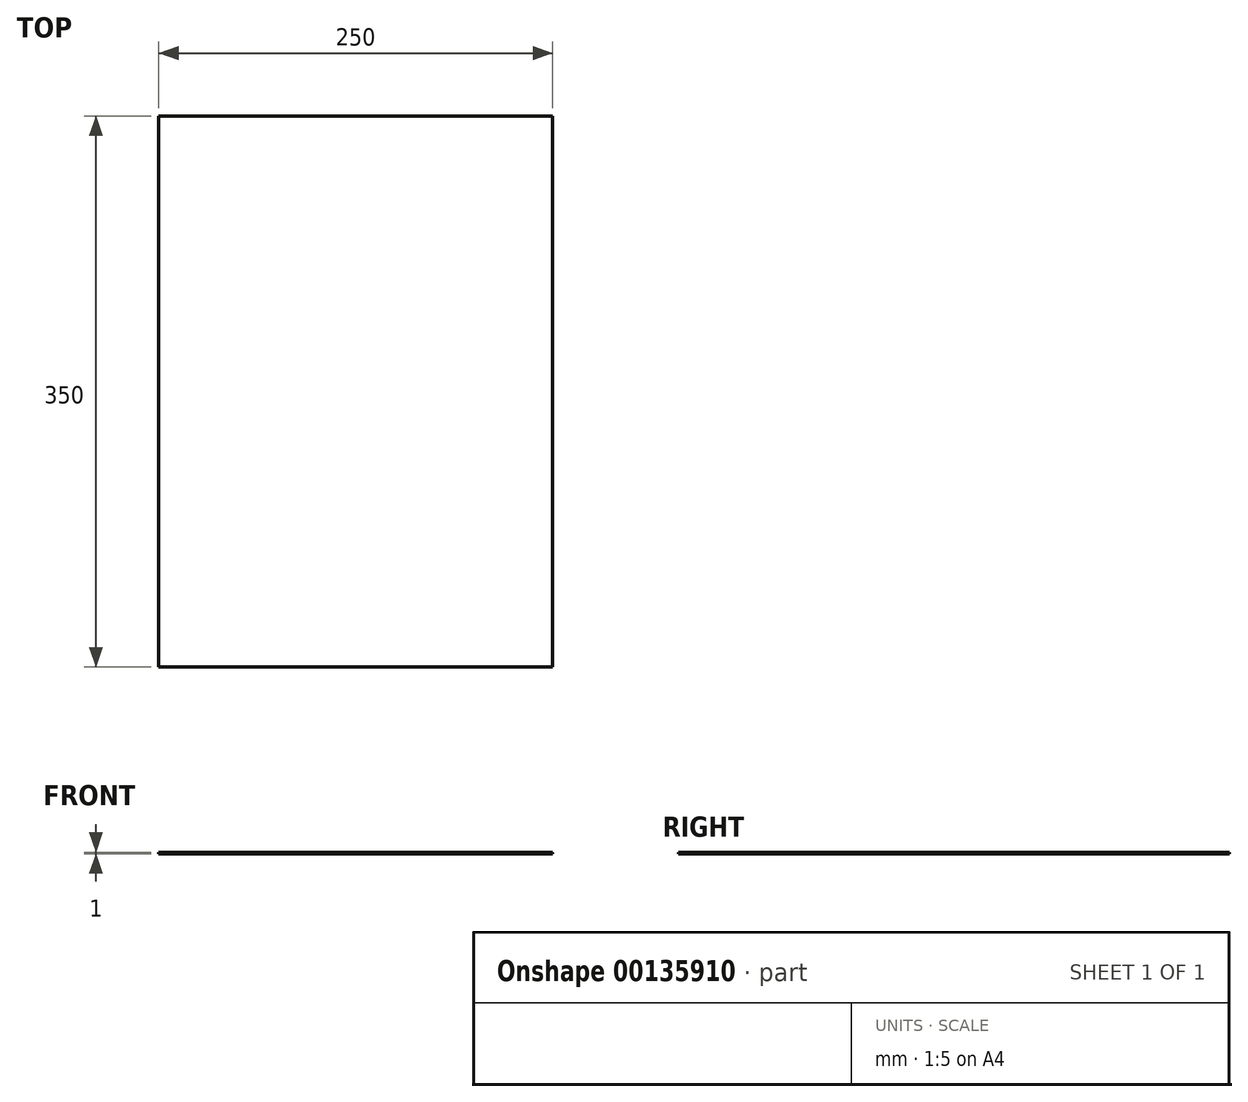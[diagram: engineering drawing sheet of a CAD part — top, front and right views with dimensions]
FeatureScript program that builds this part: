
annotation { "Feature Type Name" : "Feature", "Feature Type Description" : "" }
export const myFeature = defineFeature(function(context is Context, id is Id, definition is map)
    precondition{}
    {
        {
            var Q0;
            Q0=qCreatedBy(makeId("Top.planeOp"),FACE);
            var sketch = newSketch(context, id + "F0", { "sketchPlane" : qUnion([Q0])});
            skLineSegment(sketch, "E0.bottom", {"start": v(125, -175) * mm, "end": v(-125, -175) * mm});
            skLineSegment(sketch, "E0.top", {"start": v(125, 175) * mm, "end": v(-125, 175) * mm});
            skLineSegment(sketch, "E0.left", {"start": v(125, -175) * mm, "end": v(125, 175) * mm});
            skLineSegment(sketch, "E0.right", {"start": v(-125, -175) * mm, "end": v(-125, 175) * mm});
            skPoint(sketch, "E0.middle", {"position": v(0, 0) * mm});
            skSolve(sketch);
        }
        {
            var Q0;
            Q0 = qSketchRegion(id + "F0", true);
            extrude(context, id + "F1", {"entities" : qUnion([Q0]), "depth" : 1 * mm});
        }
    });
